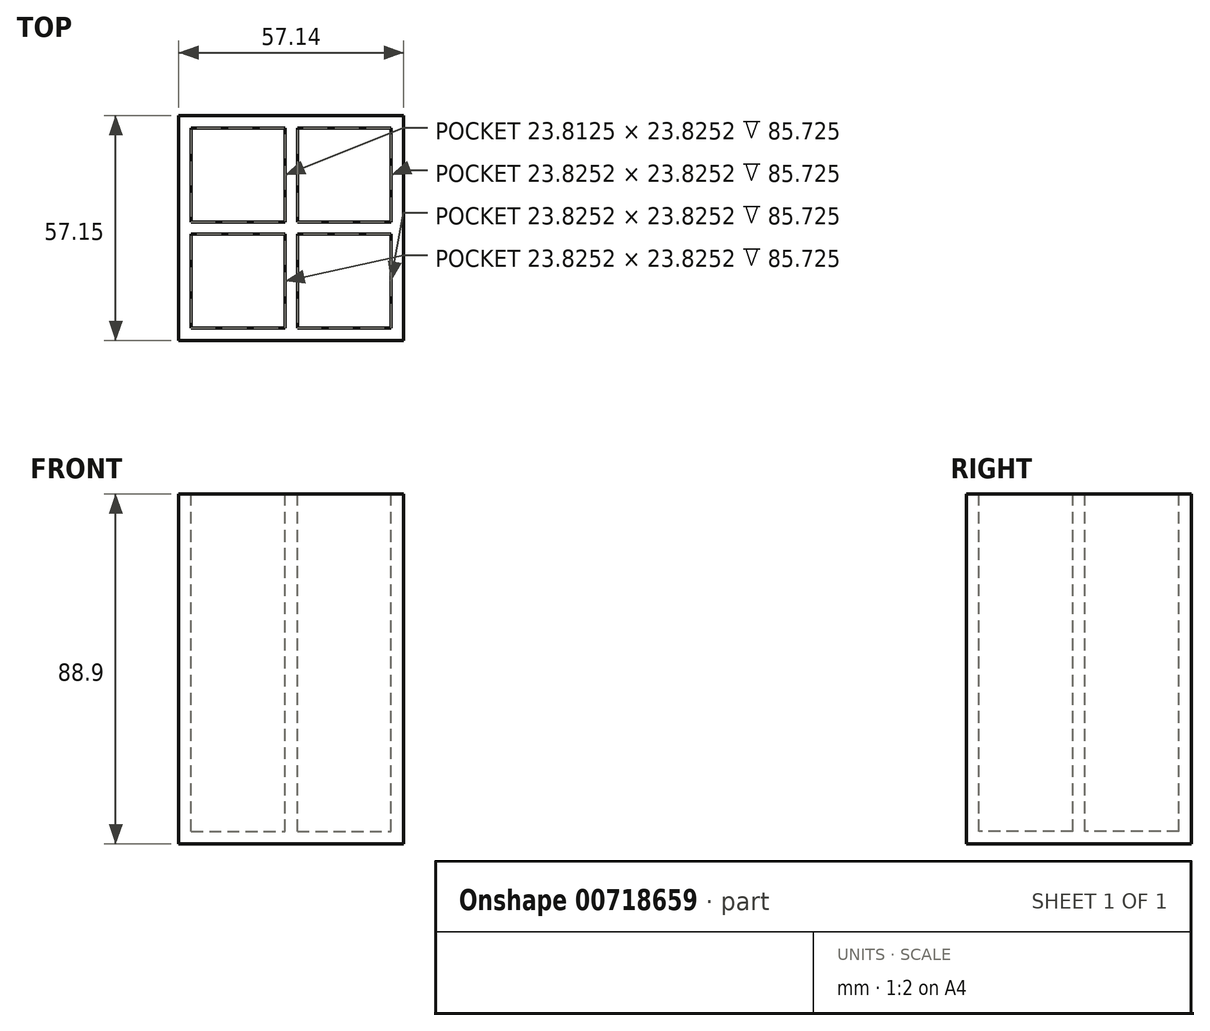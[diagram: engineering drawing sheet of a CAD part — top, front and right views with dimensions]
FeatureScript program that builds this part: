
annotation { "Feature Type Name" : "Feature", "Feature Type Description" : "" }
export const myFeature = defineFeature(function(context is Context, id is Id, definition is map)
    precondition{}
    {
        {
            var Q0;
            Q0=qCreatedBy(makeId("Front.planeOp"),FACE);
            var sketch = newSketch(context, id + "F0", { "sketchPlane" : qUnion([Q0])});
            skLineSegment(sketch, "E0.bottom", {"start": v(28.58, 42.13) * mm, "end": v(-28.58, 42.13) * mm});
            skLineSegment(sketch, "E0.top", {"start": v(28.58, -46.77) * mm, "end": v(-28.58, -46.77) * mm});
            skLineSegment(sketch, "E0.left", {"start": v(28.58, 42.13) * mm, "end": v(28.58, -46.77) * mm});
            skLineSegment(sketch, "E0.right", {"start": v(-28.58, 42.13) * mm, "end": v(-28.58, -46.77) * mm});
            skPoint(sketch, "E0.middle", {"position": v(0, -2.32) * mm});
            skSolve(sketch);
        }
        {
            var Q0;
            Q0=makeQuery(id+"F0.imprint","IMPRINT",FACE,{"disambiguationData":[TD([[makeQuery(id+"F0.imprint","IMPRINT",EDGE,{"derivedFrom":sQuery(id+"F0.wireOp",EDGE,"E0.bottom")}),1.0]])]});
            extrude(context, id + "F1", {"entities" : qUnion([Q0]), "depth" : 57.15 * mm, "offsetDistance" : 25.4 * mm});
        }
        {
            var Q0;
            Q0=makeQuery(id+"F1.opExtrude","SWEPT_FACE",FACE,{"disambiguationData":[OSD([sQuery(id+"F0.wireOp",EDGE,"E0.bottom")])]});
            var sketch = newSketch(context, id + "F2", { "sketchPlane" : qUnion([Q0])});
            skLineSegment(sketch, "E1.bottom", {"start": v(-25.4, -3.18) * mm, "end": v(-1.59, -3.18) * mm});
            skLineSegment(sketch, "E1.top", {"start": v(-25.4, -27) * mm, "end": v(-1.59, -27) * mm});
            skLineSegment(sketch, "E1.left", {"start": v(-25.4, -3.18) * mm, "end": v(-25.4, -27) * mm});
            skLineSegment(sketch, "E1.right", {"start": v(-1.59, -3.17) * mm, "end": v(-1.59, -27) * mm});
            skSolve(sketch);
        }
        {
            var Q0;
            Q0=makeQuery(id+"F2.imprint","IMPRINT",FACE,{"disambiguationData":[TD([[makeQuery(id+"F2.imprint","IMPRINT",EDGE,{"derivedFrom":sQuery(id+"F2.wireOp",EDGE,"E1.bottom")}),-1.0]])]});
            extrude(context, id + "F3", {"entities" : qUnion([Q0]), "operationType" : NewBodyOperationType.REMOVE, "oppositeDirection" : true, "depth" : 85.72 * mm, "offsetDistance" : 25.4 * mm});
        }
        {
            var Q0;
            Q0=makeQuery(id+"F1.opExtrude","SWEPT_FACE",FACE,{"disambiguationData":[OSD([sQuery(id+"F0.wireOp",EDGE,"E0.bottom")])]});
            var sketch = newSketch(context, id + "F4", { "sketchPlane" : qUnion([Q0])});
            skLineSegment(sketch, "E2.bottom", {"start": v(1.57, -3.18) * mm, "end": v(25.4, -3.18) * mm});
            skLineSegment(sketch, "E2.top", {"start": v(1.57, -27) * mm, "end": v(25.4, -27) * mm});
            skLineSegment(sketch, "E2.left", {"start": v(1.57, -3.18) * mm, "end": v(1.57, -27) * mm});
            skLineSegment(sketch, "E2.right", {"start": v(25.4, -3.17) * mm, "end": v(25.4, -27) * mm});
            skSolve(sketch);
        }
        {
            var Q0;
            Q0=makeQuery(id+"F4.imprint","IMPRINT",FACE,{"disambiguationData":[TD([[makeQuery(id+"F4.imprint","IMPRINT",EDGE,{"derivedFrom":sQuery(id+"F4.wireOp",EDGE,"E2.bottom")}),-1.0]])]});
            extrude(context, id + "F5", {"entities" : qUnion([Q0]), "operationType" : NewBodyOperationType.REMOVE, "oppositeDirection" : true, "depth" : 85.72 * mm, "offsetDistance" : 25.4 * mm});
        }
        {
            var Q0;
            Q0=makeQuery(id+"F1.opExtrude","SWEPT_FACE",FACE,{"disambiguationData":[OSD([sQuery(id+"F0.wireOp",EDGE,"E0.bottom")])]});
            var sketch = newSketch(context, id + "F6", { "sketchPlane" : qUnion([Q0])});
            skLineSegment(sketch, "E3.bottom", {"start": v(-25.4, -30.15) * mm, "end": v(-1.57, -30.15) * mm});
            skLineSegment(sketch, "E3.top", {"start": v(-25.4, -53.98) * mm, "end": v(-1.57, -53.98) * mm});
            skLineSegment(sketch, "E3.left", {"start": v(-25.4, -30.15) * mm, "end": v(-25.4, -53.98) * mm});
            skLineSegment(sketch, "E3.right", {"start": v(-1.57, -30.15) * mm, "end": v(-1.57, -53.98) * mm});
            skLineSegment(sketch, "E4.bottom", {"start": v(1.57, -30.15) * mm, "end": v(25.4, -30.15) * mm});
            skLineSegment(sketch, "E4.top", {"start": v(1.57, -53.98) * mm, "end": v(25.4, -53.98) * mm});
            skLineSegment(sketch, "E4.left", {"start": v(1.57, -30.15) * mm, "end": v(1.57, -53.98) * mm});
            skLineSegment(sketch, "E4.right", {"start": v(25.4, -30.15) * mm, "end": v(25.4, -53.98) * mm});
            skSolve(sketch);
        }
        {
            var Q0;
            Q0=makeQuery(id+"F6.imprint","IMPRINT",FACE,{"disambiguationData":[TD([[makeQuery(id+"F6.imprint","IMPRINT",EDGE,{"derivedFrom":sQuery(id+"F6.wireOp",EDGE,"E3.bottom")}),-1.0]])]});
            var Q1;
            Q1=makeQuery(id+"F6.imprint","IMPRINT",FACE,{"disambiguationData":[TD([[makeQuery(id+"F6.imprint","IMPRINT",EDGE,{"derivedFrom":sQuery(id+"F6.wireOp",EDGE,"E4.bottom")}),-1.0]])]});
            extrude(context, id + "F7", {"entities" : qUnion([Q0, Q1]), "operationType" : NewBodyOperationType.REMOVE, "oppositeDirection" : true, "depth" : 85.72 * mm, "offsetDistance" : 25.4 * mm});
        }
    });
